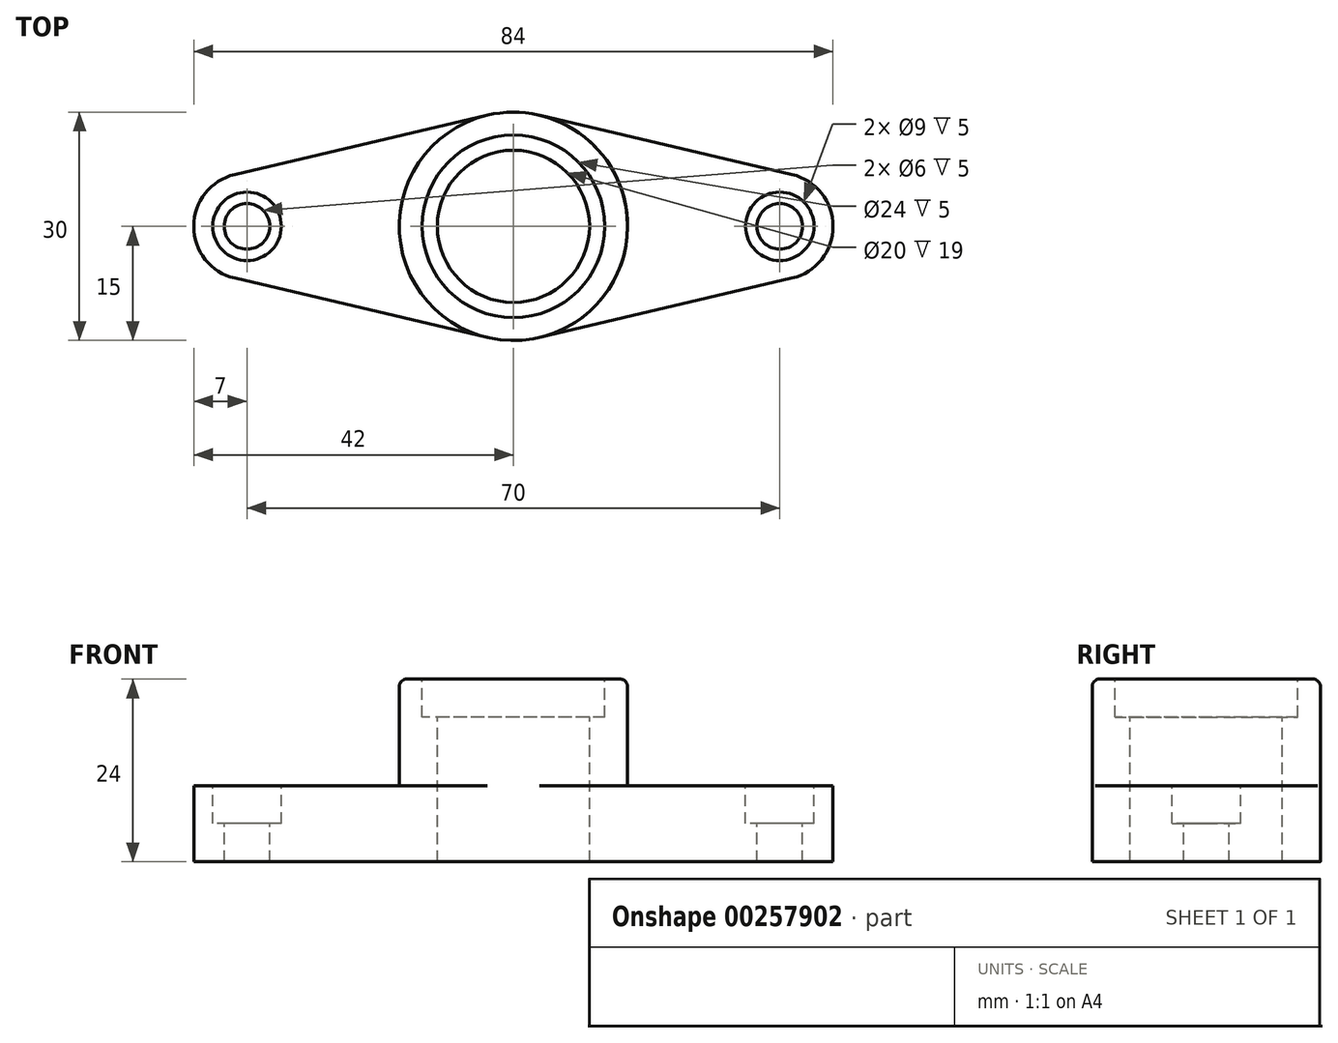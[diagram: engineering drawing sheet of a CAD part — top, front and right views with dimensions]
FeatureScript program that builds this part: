
annotation { "Feature Type Name" : "Feature", "Feature Type Description" : "" }
export const myFeature = defineFeature(function(context is Context, id is Id, definition is map)
    precondition{}
    {
        {
            var Q0;
            Q0=qCreatedBy(makeId("Top.planeOp"),FACE);
            var sketch = newSketch(context, id + "F0", { "sketchPlane" : qUnion([Q0])});
            skCircle(sketch, "E0", {"center": v(0, 0) * mm, "radius": 15 * mm});
            skCircle(sketch, "E1", {"center": v(35, 0) * mm, "radius": 7 * mm});
            skLineSegment(sketch, "E2", {"start": v(3.43, 14.6) * mm, "end": v(36.6, 6.81) * mm});
            skLineSegment(sketch, "E3", {"start": v(3.43, -14.6) * mm, "end": v(36.6, -6.81) * mm});
            skLineSegment(sketch, "E4", {"start": v(0, 33.26) * mm, "end": v(0, -26.21) * mm, "construction": true});
            skCircle(sketch, "E5.MirrorC", {"center": v(-35, 0) * mm, "radius": 7 * mm});
            skLineSegment(sketch, "E6.MirrorCS", {"start": v(-3.43, 14.6) * mm, "end": v(-36.6, 6.81) * mm});
            skLineSegment(sketch, "E7.MirrorCS", {"start": v(-3.43, -14.6) * mm, "end": v(-36.6, -6.81) * mm});
            skSolve(sketch);
        }
        {
            var Q0;
            Q0 = qSketchRegion(id + "F0", true);
            extrude(context, id + "F1", {"entities" : qUnion([Q0]), "depth" : 10 * mm});
        }
        {
            var Q0;
            Q0=makeQuery(id+"F1.opExtrude","CAP_FACE",FACE,{"disambiguationData":[OSD([sQuery(id+"F0.wireOp",EDGE,"E0"),sQuery(id+"F0.wireOp",EDGE,"E1"),sQuery(id+"F0.wireOp",EDGE,"E2"),sQuery(id+"F0.wireOp",EDGE,"E3"),sQuery(id+"F0.wireOp",EDGE,"E5.MirrorC"),sQuery(id+"F0.wireOp",EDGE,"E6.MirrorCS"),sQuery(id+"F0.wireOp",EDGE,"E7.MirrorCS")])],"isStart":false});
            var sketch = newSketch(context, id + "F2", { "sketchPlane" : qUnion([Q0])});
            skCircle(sketch, "E8", {"center": v(0, 0) * mm, "radius": 15 * mm});
            skSolve(sketch);
        }
        {
            var Q0;
            Q0 = qSketchRegion(id + "F2", true);
            extrude(context, id + "F3", {"entities" : qUnion([Q0]), "operationType" : NewBodyOperationType.ADD, "depth" : 14 * mm});
        }
        {
            var Q0;
            {var subQ0=sQuery(id+"F0.wireOp",EDGE,"E5.MirrorC");var subQ1=sQuery(id+"F0.wireOp",EDGE,"E6.MirrorCS");var subQ2=sQuery(id+"F0.wireOp",EDGE,"E3");var subQ3=sQuery(id+"F0.wireOp",EDGE,"E0");var subQ4=sQuery(id+"F0.wireOp",EDGE,"E7.MirrorCS");var subQ5=sQuery(id+"F0.wireOp",EDGE,"E2");Q0=makeQuery(id+"F3.boolean.opBoolean","SPLIT",FACE,{"disambiguationData":[TD([makeQuery(id+"F1.opExtrude","SWEPT_FACE",FACE,{"disambiguationData":[OSD([subQ0])]})])],"derivedFrom":makeQuery(id+"F1.opExtrude","CAP_FACE",FACE,{"disambiguationData":[OSD([subQ3,sQuery(id+"F0.wireOp",EDGE,"E1"),subQ5,subQ2,subQ0,subQ1,subQ4])],"isStart":false})});}
            var sketch = newSketch(context, id + "F4", { "sketchPlane" : qUnion([Q0])});
            skCircle(sketch, "E9", {"center": v(-35, 0) * mm, "radius": 4.5 * mm});
            skCircle(sketch, "E10", {"center": v(35, 0) * mm, "radius": 4.5 * mm});
            skSolve(sketch);
        }
        {
            var Q0;
            Q0 = qSketchRegion(id + "F4", true);
            extrude(context, id + "F5", {"entities" : qUnion([Q0]), "oppositeDirection" : true, "depth" : 5 * mm});
        }
        {
            var Q0;
            Q0=makeQuery(id+"F5.opExtrude","SWEPT_BODY",BODY,{"disambiguationData":[OSD([sQuery(id+"F4.wireOp",EDGE,"E9")])]});
            var Q1;
            Q1=makeQuery(id+"F5.opExtrude","SWEPT_BODY",BODY,{"disambiguationData":[OSD([sQuery(id+"F4.wireOp",EDGE,"E10")])]});
            var Q2;
            Q2=makeQuery(id+"F1.opExtrude","SWEPT_BODY",BODY,{"disambiguationData":[OSD([sQuery(id+"F0.wireOp",EDGE,"E0"),sQuery(id+"F0.wireOp",EDGE,"E1"),sQuery(id+"F0.wireOp",EDGE,"E2"),sQuery(id+"F0.wireOp",EDGE,"E3"),sQuery(id+"F0.wireOp",EDGE,"E5.MirrorC"),sQuery(id+"F0.wireOp",EDGE,"E6.MirrorCS"),sQuery(id+"F0.wireOp",EDGE,"E7.MirrorCS")])]});
            booleanBodies(context, id + "F6", {"operationType" : BooleanOperationType.SUBTRACTION, "tools" : qUnion([Q0, Q1]), "targets" : qUnion([Q2])});
        }
        {
            var Q0;
            Q0=makeQuery(id+"F6.opBoolean","COPY",FACE,{"derivedFrom":makeQuery(id+"F5.opExtrude","CAP_FACE",FACE,{"disambiguationData":[OSD([sQuery(id+"F4.wireOp",EDGE,"E9")])],"isStart":false})});
            var sketch = newSketch(context, id + "F7", { "sketchPlane" : qUnion([Q0])});
            skCircle(sketch, "E11", {"center": v(-35, 0) * mm, "radius": 3 * mm});
            skLineSegment(sketch, "E12", {"start": v(0, 33.24) * mm, "end": v(0, -45.45) * mm, "construction": true});
            skCircle(sketch, "E13.MirrorC", {"center": v(35, 0) * mm, "radius": 3 * mm});
            skSolve(sketch);
        }
        {
            var Q0;
            Q0 = qSketchRegion(id + "F7", true);
            extrude(context, id + "F8", {"entities" : qUnion([Q0]), "oppositeDirection" : true, "depth" : 27.2 * mm});
        }
        {
            var Q0;
            Q0=makeQuery(id+"F8.opExtrude","SWEPT_BODY",BODY,{"disambiguationData":[OSD([sQuery(id+"F7.wireOp",EDGE,"E11")])]});
            var Q1;
            Q1=makeQuery(id+"F8.opExtrude","SWEPT_BODY",BODY,{"disambiguationData":[OSD([sQuery(id+"F7.wireOp",EDGE,"E13.MirrorC")])]});
            var Q2;
            Q2=makeQuery(id+"F1.opExtrude","SWEPT_BODY",BODY,{"disambiguationData":[OSD([sQuery(id+"F0.wireOp",EDGE,"E0"),sQuery(id+"F0.wireOp",EDGE,"E1"),sQuery(id+"F0.wireOp",EDGE,"E2"),sQuery(id+"F0.wireOp",EDGE,"E3"),sQuery(id+"F0.wireOp",EDGE,"E5.MirrorC"),sQuery(id+"F0.wireOp",EDGE,"E6.MirrorCS"),sQuery(id+"F0.wireOp",EDGE,"E7.MirrorCS")])]});
            booleanBodies(context, id + "F9", {"operationType" : BooleanOperationType.SUBTRACTION, "tools" : qUnion([Q0, Q1]), "targets" : qUnion([Q2])});
        }
        {
            var Q0;
            Q0=makeQuery(id+"F3.opExtrude","CAP_FACE",FACE,{"disambiguationData":[OSD([sQuery(id+"F2.wireOp",EDGE,"E8")])],"isStart":false});
            var sketch = newSketch(context, id + "F10", { "sketchPlane" : qUnion([Q0])});
            skCircle(sketch, "E14", {"center": v(0, 0) * mm, "radius": 12 * mm});
            skSolve(sketch);
        }
        {
            var Q0;
            Q0 = qSketchRegion(id + "F10", true);
            extrude(context, id + "F11", {"entities" : qUnion([Q0]), "oppositeDirection" : true, "depth" : 5 * mm});
        }
        {
            var Q0;
            Q0=makeQuery(id+"F11.opExtrude","SWEPT_BODY",BODY,{"disambiguationData":[OSD([sQuery(id+"F10.wireOp",EDGE,"E14")])]});
            var Q1;
            Q1=makeQuery(id+"F1.opExtrude","SWEPT_BODY",BODY,{"disambiguationData":[OSD([sQuery(id+"F0.wireOp",EDGE,"E0"),sQuery(id+"F0.wireOp",EDGE,"E1"),sQuery(id+"F0.wireOp",EDGE,"E2"),sQuery(id+"F0.wireOp",EDGE,"E3"),sQuery(id+"F0.wireOp",EDGE,"E5.MirrorC"),sQuery(id+"F0.wireOp",EDGE,"E6.MirrorCS"),sQuery(id+"F0.wireOp",EDGE,"E7.MirrorCS")])]});
            booleanBodies(context, id + "F12", {"operationType" : BooleanOperationType.SUBTRACTION, "tools" : qUnion([Q0]), "targets" : qUnion([Q1])});
        }
        {
            var Q0;
            Q0=makeQuery(id+"F12.opBoolean","COPY",FACE,{"derivedFrom":makeQuery(id+"F11.opExtrude","CAP_FACE",FACE,{"disambiguationData":[OSD([sQuery(id+"F10.wireOp",EDGE,"E14")])],"isStart":false})});
            var sketch = newSketch(context, id + "F13", { "sketchPlane" : qUnion([Q0])});
            skCircle(sketch, "E15", {"center": v(0, 0) * mm, "radius": 10 * mm});
            skSolve(sketch);
        }
        {
            var Q0;
            Q0=makeQuery(id+"F13.imprint","IMPRINT",FACE,{"disambiguationData":[TD([[makeQuery(id+"F13.imprint","IMPRINT",EDGE,{"derivedFrom":sQuery(id+"F13.wireOp",EDGE,"E15")}),1.0]])]});
            extrude(context, id + "F14", {"entities" : qUnion([Q0]), "oppositeDirection" : true, "depth" : 25 * mm});
        }
        {
            var Q0;
            Q0=makeQuery(id+"F14.opExtrude","SWEPT_BODY",BODY,{"disambiguationData":[OSD([sQuery(id+"F13.wireOp",EDGE,"E15")])]});
            var Q1;
            Q1=makeQuery(id+"F1.opExtrude","SWEPT_BODY",BODY,{"disambiguationData":[OSD([sQuery(id+"F0.wireOp",EDGE,"E0"),sQuery(id+"F0.wireOp",EDGE,"E1"),sQuery(id+"F0.wireOp",EDGE,"E2"),sQuery(id+"F0.wireOp",EDGE,"E3"),sQuery(id+"F0.wireOp",EDGE,"E5.MirrorC"),sQuery(id+"F0.wireOp",EDGE,"E6.MirrorCS"),sQuery(id+"F0.wireOp",EDGE,"E7.MirrorCS")])]});
            booleanBodies(context, id + "F15", {"operationType" : BooleanOperationType.SUBTRACTION, "tools" : qUnion([Q0]), "targets" : qUnion([Q1])});
        }
        {
            var Q0;
            Q0=makeQuery(id+"F3.opExtrude","CAP_EDGE",EDGE,{"disambiguationData":[OSD([sQuery(id+"F2.wireOp",EDGE,"E8")])],"isStart":false});
            fillet(context, id + "F16", {"entities" : qUnion([Q0]), "radius" : 1 * mm, "tangentPropagation" : true, "allowEdgeOverflow" : false});
        }
    });
